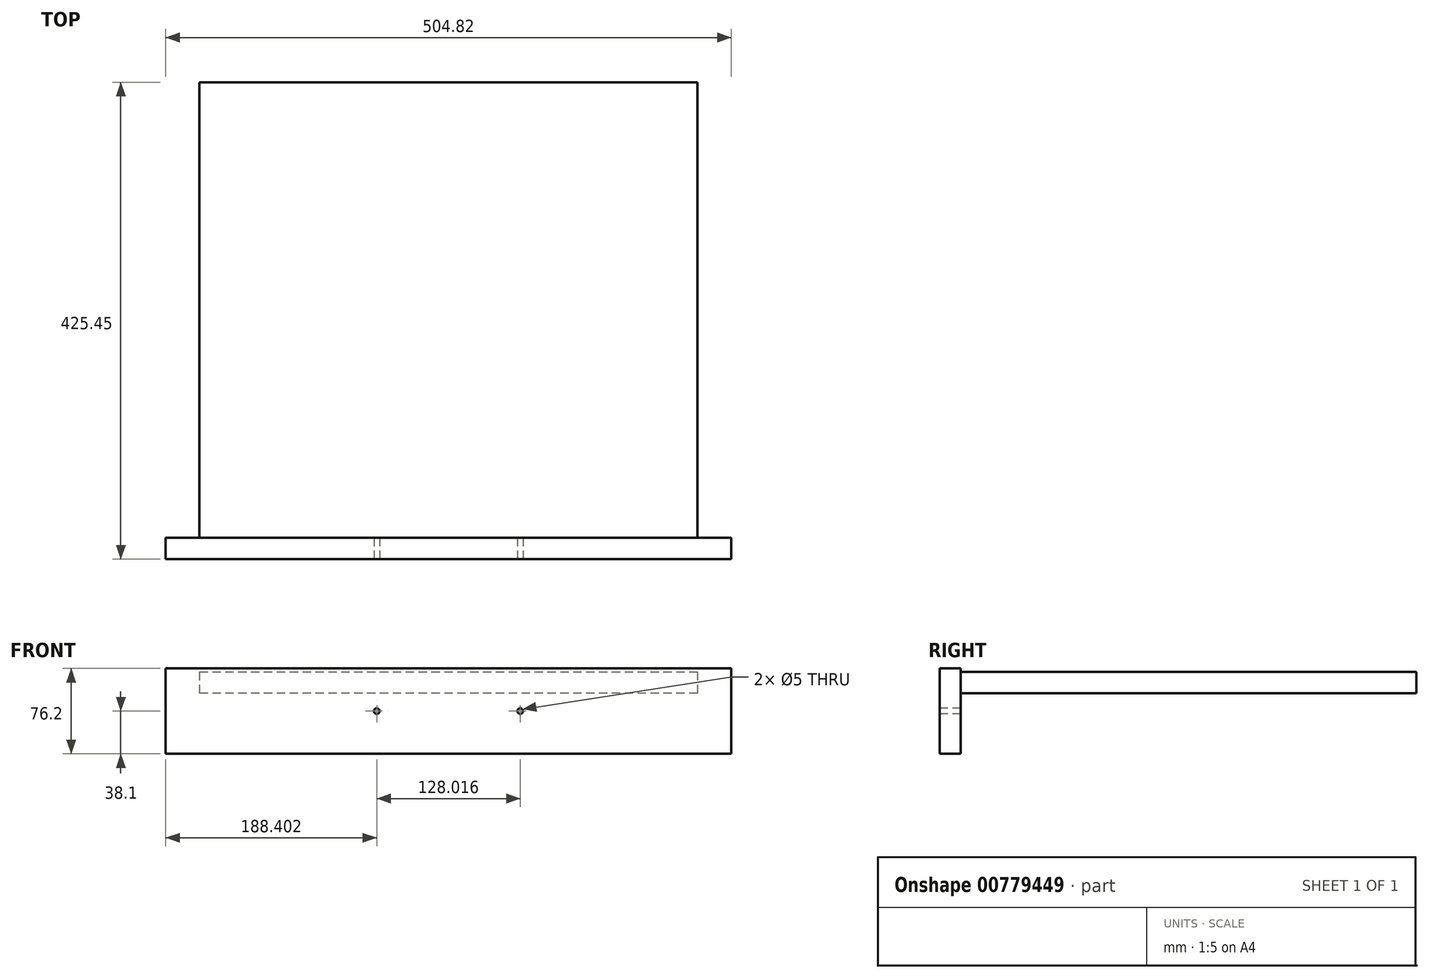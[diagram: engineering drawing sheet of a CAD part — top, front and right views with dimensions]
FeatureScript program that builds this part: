
annotation { "Feature Type Name" : "Feature", "Feature Type Description" : "" }
export const myFeature = defineFeature(function(context is Context, id is Id, definition is map)
    precondition{}
    {
        {
            var Q0;
            Q0=qCreatedBy(makeId("Front.planeOp"),FACE);
            var sketch = newSketch(context, id + "F0", { "sketchPlane" : qUnion([Q0])});
            skLineSegment(sketch, "E0.bottom", {"start": v(-252.41, 38.1) * mm, "end": v(252.41, 38.1) * mm});
            skLineSegment(sketch, "E0.top", {"start": v(-252.41, -38.1) * mm, "end": v(252.41, -38.1) * mm});
            skLineSegment(sketch, "E0.left", {"start": v(-252.41, 38.1) * mm, "end": v(-252.41, -38.1) * mm});
            skLineSegment(sketch, "E0.right", {"start": v(252.41, 38.1) * mm, "end": v(252.41, -38.1) * mm});
            skPoint(sketch, "E0.middle", {"position": v(0, 0) * mm});
            skSolve(sketch);
        }
        {
            var Q0;
            Q0=makeQuery(id+"F0.imprint","IMPRINT",FACE,{"disambiguationData":[TD([[makeQuery(id+"F0.imprint","IMPRINT",EDGE,{"derivedFrom":sQuery(id+"F0.wireOp",EDGE,"E0.bottom")}),-1.0]])]});
            extrude(context, id + "F1", {"entities" : qUnion([Q0]), "depth" : 19.05 * mm, "offsetDistance" : 25.4 * mm});
        }
        {
            var Q0;
            Q0=makeQuery(id+"F1.opExtrude","CAP_FACE",FACE,{"disambiguationData":[OSD([sQuery(id+"F0.wireOp",EDGE,"E0.bottom"),sQuery(id+"F0.wireOp",EDGE,"E0.top"),sQuery(id+"F0.wireOp",EDGE,"E0.left"),sQuery(id+"F0.wireOp",EDGE,"E0.right")])],"isStart":false});
            var sketch = newSketch(context, id + "F2", { "sketchPlane" : qUnion([Q0])});
            skLineSegment(sketch, "E1", {"start": v(0, 0) * mm, "end": v(-64, 0) * mm});
            skLineSegment(sketch, "E2", {"start": v(0, 0) * mm, "end": v(64, 0) * mm});
            skPoint(sketch, "E3", {"position": v(-64, 0) * mm});
            skPoint(sketch, "E4", {"position": v(64, 0) * mm});
            skSolve(sketch);
        }
        {
            var Q0;
            Q0=sQuery(id+"F2.wireOp",VERTEX,"E3");
            var Q1;
            Q1=sQuery(id+"F2.wireOp",VERTEX,"E4");
            var Q2;
            Q2=makeQuery(id+"F1.opExtrude","SWEPT_BODY",BODY,{"disambiguationData":[OSD([sQuery(id+"F0.wireOp",EDGE,"E0.bottom"),sQuery(id+"F0.wireOp",EDGE,"E0.top"),sQuery(id+"F0.wireOp",EDGE,"E0.left"),sQuery(id+"F0.wireOp",EDGE,"E0.right")])]});
            hole(context, id + "F3", {"style" : HoleStyle.SIMPLE, "endStyle" : HoleEndStyle.BLIND, "holeDiameter" : 5 * mm, "majorDiameter" : 6.35 * mm, "holeDepth" : 25.4 * mm, "isTappedThrough" : true, "tappedDepth" : 12.7 * mm, "tapClearance" : 3, "startFromSketch" : true, "locations" : qUnion([Q0, Q1]), "scope" : qUnion([Q2])});
        }
        {
            var Q0;
            Q0=makeQuery(id+"F1.opExtrude","CAP_FACE",FACE,{"disambiguationData":[OSD([sQuery(id+"F0.wireOp",EDGE,"E0.bottom"),sQuery(id+"F0.wireOp",EDGE,"E0.top"),sQuery(id+"F0.wireOp",EDGE,"E0.left"),sQuery(id+"F0.wireOp",EDGE,"E0.right")])],"isStart":true});
            var sketch = newSketch(context, id + "F4", { "sketchPlane" : qUnion([Q0])});
            skLineSegment(sketch, "E5", {"start": v(0, 38.1) * mm, "end": v(0, 34.93) * mm});
            skLineSegment(sketch, "E6", {"start": v(0, 34.93) * mm, "end": v(-222.25, 34.93) * mm});
            skLineSegment(sketch, "E7.bottom", {"start": v(-222.25, 34.93) * mm, "end": v(222.25, 34.93) * mm});
            skLineSegment(sketch, "E7.top", {"start": v(-222.25, 15.88) * mm, "end": v(222.25, 15.88) * mm});
            skLineSegment(sketch, "E7.left", {"start": v(-222.25, 34.93) * mm, "end": v(-222.25, 15.88) * mm});
            skLineSegment(sketch, "E7.right", {"start": v(222.25, 34.93) * mm, "end": v(222.25, 15.88) * mm});
            skSolve(sketch);
        }
        {
            var Q0;
            Q0=makeQuery(id+"F4.imprint","IMPRINT",FACE,{"disambiguationData":[TD([[makeQuery(id+"F4.imprint","IMPRINT",EDGE,{"derivedFrom":sQuery(id+"F4.wireOp",EDGE,"E7.top")}),1.0]])]});
            extrude(context, id + "F5", {"entities" : qUnion([Q0]), "operationType" : NewBodyOperationType.ADD, "depth" : 406.4 * mm, "offsetDistance" : 25.4 * mm});
        }
    });
